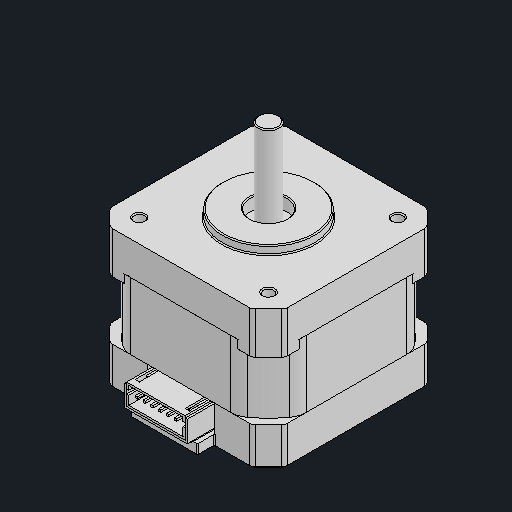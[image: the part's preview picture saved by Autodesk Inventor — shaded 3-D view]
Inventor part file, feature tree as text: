
AUTODESK INVENTOR PART (.ipt)
format: ipt  version: 2024.2 (Build 282272000, 272)  size: 436,224 bytes
history: native  units: mm
features: other x7, fillet x2, extrude x1
ambient origin geometry x8: Origin, YZ Plane, XZ Plane, XY Plane, X Axis, Y Axis, Z Axis, Center Point
bodies: Body1 (feature_tree), Body2 (feature_tree), Body3 (feature_tree), Body4 (feature_tree), Body5 (feature_tree)
feature tree (10):
  other  "솔리드1"
  other  "솔리드2"
  other  "솔리드3"
  other  "솔리드4"
  other  "솔리드5"
  fillet  "Fillet6"  [1 undecoded]
  other  "M3x0.5 Tapped Hole1"
  fillet  "Fillet11"  [1 undecoded]
  extrude  "Extrude-Thin1"  [1 undecoded]
  other  "Boss-Extrude14"
note: 3 required parameter values undecoded (feature->parameter linkage not recoverable at this tier; creation-order binding heuristic only, values carry confidence <= 0.55)
